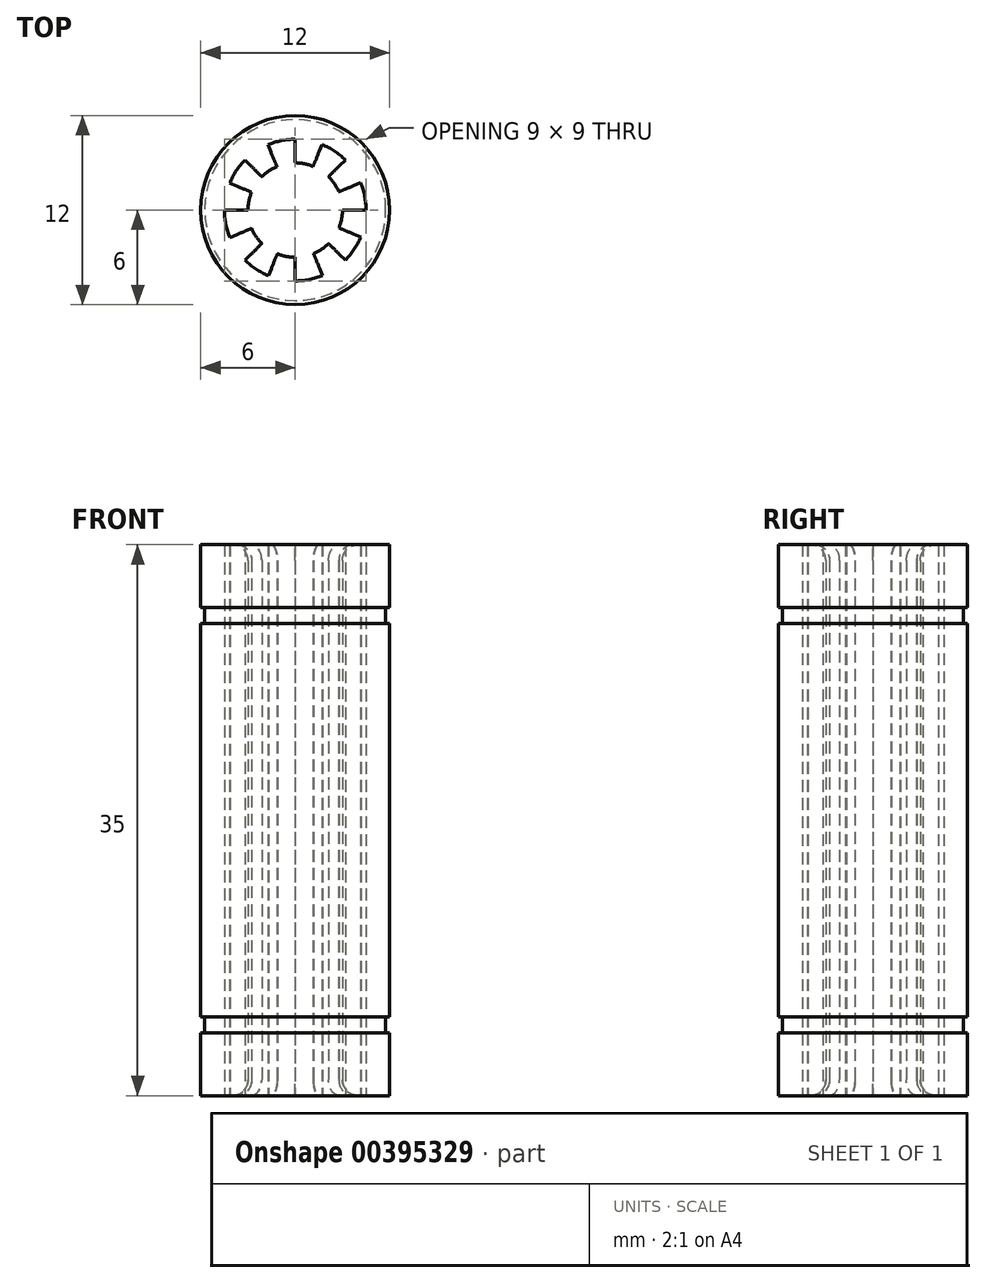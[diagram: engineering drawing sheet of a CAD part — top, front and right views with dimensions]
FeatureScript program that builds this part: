
annotation { "Feature Type Name" : "Feature", "Feature Type Description" : "" }
export const myFeature = defineFeature(function(context is Context, id is Id, definition is map)
    precondition{}
    {
        {
            var Q0;
            Q0=qCreatedBy(makeId("Top.planeOp"),FACE);
            var sketch = newSketch(context, id + "F0", { "sketchPlane" : qUnion([Q0])});
            skCircle(sketch, "E0", {"center": v(0, 0) * mm, "radius": 3 * mm});
            skCircle(sketch, "E1", {"center": v(0, 0) * mm, "radius": 6 * mm});
            skCircle(sketch, "E2", {"center": v(0, 0) * mm, "radius": 4.5 * mm});
            skLineSegment(sketch, "E3", {"start": v(0, 6) * mm, "end": v(0, -6) * mm});
            skLineSegment(sketch, "E4", {"start": v(-6, 0) * mm, "end": v(6, 0) * mm});
            skPoint(sketch, "E5", {"position": v(4.56, 3.9) * mm});
            skPoint(sketch, "E6", {"position": v(-4.24, 4.24) * mm});
            skPoint(sketch, "E7", {"position": v(-4.52, -3.95) * mm});
            skPoint(sketch, "E8", {"position": v(4.86, -3.52) * mm});
            skLineSegment(sketch, "E9", {"start": v(0, 0) * mm, "end": v(-4.24, 4.24) * mm});
            skPoint(sketch, "E10", {"position": v(-2.32, 5.53) * mm});
            skPoint(sketch, "E11", {"position": v(-5.54, 2.3) * mm});
            skLineSegment(sketch, "E12", {"start": v(-5.54, 2.3) * mm, "end": v(0, 0) * mm});
            skLineSegment(sketch, "E13", {"start": v(-2.32, 5.53) * mm, "end": v(0, 0) * mm});
            skSolve(sketch);
        }
        {
            var Q0;
            {var subQ0=sQuery(id+"F0.wireOp",EDGE,"E3");var subQ1=sQuery(id+"F0.wireOp",EDGE,"E1");var subQ2=makeQuery(id+"F0.imprint","INTERSECT",VERTEX,{"disambiguationData":[OD(0.0)],"derivedFrom":[subQ1,subQ0]});Q0=makeQuery(id+"F0.imprint","IMPRINT",FACE,{"disambiguationData":[TD([[makeQuery(id+"F0.imprint","IMPRINT",EDGE,{"disambiguationData":[TD([[subQ2,-1.0]])],"derivedFrom":subQ1}),1.0]])]});}
            var Q1;
            {var subQ0=sQuery(id+"F0.wireOp",EDGE,"E13");var subQ1=sQuery(id+"F0.wireOp",EDGE,"E0");var subQ2=makeQuery(id+"F0.imprint","INTERSECT",VERTEX,{"derivedFrom":[subQ1,subQ0]});Q1=makeQuery(id+"F0.imprint","IMPRINT",FACE,{"disambiguationData":[TD([[makeQuery(id+"F0.imprint","IMPRINT",EDGE,{"disambiguationData":[TD([[subQ2,-1.0]])],"derivedFrom":subQ1}),-1.0]])]});}
            var Q2;
            {var subQ0=sQuery(id+"F0.wireOp",EDGE,"E9");var subQ1=sQuery(id+"F0.wireOp",EDGE,"E1");var subQ2=makeQuery(id+"F0.imprint","INTERSECT",VERTEX,{"derivedFrom":[subQ1,subQ0]});Q2=makeQuery(id+"F0.imprint","IMPRINT",FACE,{"disambiguationData":[TD([[makeQuery(id+"F0.imprint","IMPRINT",EDGE,{"disambiguationData":[TD([[subQ2,1.0]])],"derivedFrom":subQ1}),1.0]])]});}
            extrude(context, id + "F1", {"entities" : qUnion([Q0, Q1, Q2]), "depth" : 35 * mm});
        }
        {
            var Q0;
            Q0=qCreatedBy(makeId("Front.planeOp"),FACE);
            var sketch = newSketch(context, id + "F2", { "sketchPlane" : qUnion([Q0])});
            skLineSegment(sketch, "E14", {"start": v(0, 46.48) * mm, "end": v(0, -20.09) * mm, "construction": true});
            skSolve(sketch);
        }
        {
            var Q0;
            Q0=makeQuery(id+"F1.opExtrude","SWEPT_BODY",BODY,{"disambiguationData":[OSD([sQuery(id+"F0.wireOp",EDGE,"E0"),sQuery(id+"F0.wireOp",EDGE,"E1"),sQuery(id+"F0.wireOp",EDGE,"E2"),sQuery(id+"F0.wireOp",EDGE,"E3"),sQuery(id+"F0.wireOp",EDGE,"E4"),sQuery(id+"F0.wireOp",EDGE,"E9")])]});
            var Q1;
            Q1=sQuery(id+"F2.wireOp",EDGE,"E14");
            circularPattern(context, id + "F3", {"entities" : qUnion([Q0]), "axis" : qUnion([Q1]), "angle" : 360 * degree, "instanceCount" : 8, "oppositeDirection" : true, "equalSpace" : true});
        }
        {
            var Q0;
            Q0=makeQuery(id+"F1.opExtrude","SWEPT_BODY",BODY,{"disambiguationData":[OSD([sQuery(id+"F0.wireOp",EDGE,"E0"),sQuery(id+"F0.wireOp",EDGE,"E1"),sQuery(id+"F0.wireOp",EDGE,"E2"),sQuery(id+"F0.wireOp",EDGE,"E3"),sQuery(id+"F0.wireOp",EDGE,"E9"),sQuery(id+"F0.wireOp",EDGE,"E13")])]});
            var Q1;
            Q1=makeQuery(id+"F3.opPattern","COPY",BODY,{"derivedFrom":makeQuery(id+"F1.opExtrude","SWEPT_BODY",BODY,{"disambiguationData":[OSD([sQuery(id+"F0.wireOp",EDGE,"E0"),sQuery(id+"F0.wireOp",EDGE,"E1"),sQuery(id+"F0.wireOp",EDGE,"E2"),sQuery(id+"F0.wireOp",EDGE,"E3"),sQuery(id+"F0.wireOp",EDGE,"E9"),sQuery(id+"F0.wireOp",EDGE,"E13")])]}),"instanceName":"1"});
            var Q2;
            Q2=makeQuery(id+"F3.opPattern","COPY",BODY,{"derivedFrom":makeQuery(id+"F1.opExtrude","SWEPT_BODY",BODY,{"disambiguationData":[OSD([sQuery(id+"F0.wireOp",EDGE,"E0"),sQuery(id+"F0.wireOp",EDGE,"E1"),sQuery(id+"F0.wireOp",EDGE,"E2"),sQuery(id+"F0.wireOp",EDGE,"E3"),sQuery(id+"F0.wireOp",EDGE,"E9"),sQuery(id+"F0.wireOp",EDGE,"E13")])]}),"instanceName":"2"});
            var Q3;
            Q3=makeQuery(id+"F3.opPattern","COPY",BODY,{"derivedFrom":makeQuery(id+"F1.opExtrude","SWEPT_BODY",BODY,{"disambiguationData":[OSD([sQuery(id+"F0.wireOp",EDGE,"E0"),sQuery(id+"F0.wireOp",EDGE,"E1"),sQuery(id+"F0.wireOp",EDGE,"E2"),sQuery(id+"F0.wireOp",EDGE,"E3"),sQuery(id+"F0.wireOp",EDGE,"E9"),sQuery(id+"F0.wireOp",EDGE,"E13")])]}),"instanceName":"3"});
            var Q4;
            Q4=makeQuery(id+"F3.opPattern","COPY",BODY,{"derivedFrom":makeQuery(id+"F1.opExtrude","SWEPT_BODY",BODY,{"disambiguationData":[OSD([sQuery(id+"F0.wireOp",EDGE,"E0"),sQuery(id+"F0.wireOp",EDGE,"E1"),sQuery(id+"F0.wireOp",EDGE,"E2"),sQuery(id+"F0.wireOp",EDGE,"E3"),sQuery(id+"F0.wireOp",EDGE,"E9"),sQuery(id+"F0.wireOp",EDGE,"E13")])]}),"instanceName":"4"});
            var Q5;
            Q5=makeQuery(id+"F3.opPattern","COPY",BODY,{"derivedFrom":makeQuery(id+"F1.opExtrude","SWEPT_BODY",BODY,{"disambiguationData":[OSD([sQuery(id+"F0.wireOp",EDGE,"E0"),sQuery(id+"F0.wireOp",EDGE,"E1"),sQuery(id+"F0.wireOp",EDGE,"E2"),sQuery(id+"F0.wireOp",EDGE,"E3"),sQuery(id+"F0.wireOp",EDGE,"E9"),sQuery(id+"F0.wireOp",EDGE,"E13")])]}),"instanceName":"5"});
            var Q6;
            Q6=makeQuery(id+"F3.opPattern","COPY",BODY,{"derivedFrom":makeQuery(id+"F1.opExtrude","SWEPT_BODY",BODY,{"disambiguationData":[OSD([sQuery(id+"F0.wireOp",EDGE,"E0"),sQuery(id+"F0.wireOp",EDGE,"E1"),sQuery(id+"F0.wireOp",EDGE,"E2"),sQuery(id+"F0.wireOp",EDGE,"E3"),sQuery(id+"F0.wireOp",EDGE,"E9"),sQuery(id+"F0.wireOp",EDGE,"E13")])]}),"instanceName":"6"});
            var Q7;
            Q7=makeQuery(id+"F3.opPattern","COPY",BODY,{"derivedFrom":makeQuery(id+"F1.opExtrude","SWEPT_BODY",BODY,{"disambiguationData":[OSD([sQuery(id+"F0.wireOp",EDGE,"E0"),sQuery(id+"F0.wireOp",EDGE,"E1"),sQuery(id+"F0.wireOp",EDGE,"E2"),sQuery(id+"F0.wireOp",EDGE,"E3"),sQuery(id+"F0.wireOp",EDGE,"E9"),sQuery(id+"F0.wireOp",EDGE,"E13")])]}),"instanceName":"7"});
            booleanBodies(context, id + "F4", {"operationType" : BooleanOperationType.UNION, "tools" : qUnion([Q0, Q1, Q2, Q3, Q4, Q5, Q6, Q7])});
        }
        {
            var Q0;
            Q0=makeQuery(id+"F3.opPattern","COPY",EDGE,{"derivedFrom":makeQuery(id+"F1.opExtrude","CAP_EDGE",EDGE,{"disambiguationData":[OSD([sQuery(id+"F0.wireOp",EDGE,"E0")])],"isStart":false}),"instanceName":"1"});
            var Q1;
            Q1=makeQuery(id+"F1.opExtrude","CAP_EDGE",EDGE,{"disambiguationData":[OSD([sQuery(id+"F0.wireOp",EDGE,"E0")])],"isStart":false});
            var Q2;
            Q2=makeQuery(id+"F3.opPattern","COPY",EDGE,{"derivedFrom":makeQuery(id+"F1.opExtrude","CAP_EDGE",EDGE,{"disambiguationData":[OSD([sQuery(id+"F0.wireOp",EDGE,"E0")])],"isStart":false}),"instanceName":"7"});
            var Q3;
            Q3=makeQuery(id+"F3.opPattern","COPY",EDGE,{"derivedFrom":makeQuery(id+"F1.opExtrude","CAP_EDGE",EDGE,{"disambiguationData":[OSD([sQuery(id+"F0.wireOp",EDGE,"E0")])],"isStart":false}),"instanceName":"6"});
            var Q4;
            Q4=makeQuery(id+"F3.opPattern","COPY",EDGE,{"derivedFrom":makeQuery(id+"F1.opExtrude","CAP_EDGE",EDGE,{"disambiguationData":[OSD([sQuery(id+"F0.wireOp",EDGE,"E0")])],"isStart":false}),"instanceName":"5"});
            var Q5;
            Q5=makeQuery(id+"F3.opPattern","COPY",EDGE,{"derivedFrom":makeQuery(id+"F1.opExtrude","CAP_EDGE",EDGE,{"disambiguationData":[OSD([sQuery(id+"F0.wireOp",EDGE,"E0")])],"isStart":false}),"instanceName":"4"});
            var Q6;
            Q6=makeQuery(id+"F3.opPattern","COPY",EDGE,{"derivedFrom":makeQuery(id+"F1.opExtrude","CAP_EDGE",EDGE,{"disambiguationData":[OSD([sQuery(id+"F0.wireOp",EDGE,"E0")])],"isStart":false}),"instanceName":"3"});
            var Q7;
            Q7=makeQuery(id+"F3.opPattern","COPY",EDGE,{"derivedFrom":makeQuery(id+"F1.opExtrude","CAP_EDGE",EDGE,{"disambiguationData":[OSD([sQuery(id+"F0.wireOp",EDGE,"E0")])],"isStart":false}),"instanceName":"2"});
            var Q8;
            Q8=makeQuery(id+"F3.opPattern","COPY",EDGE,{"derivedFrom":makeQuery(id+"F1.opExtrude","CAP_EDGE",EDGE,{"disambiguationData":[OSD([sQuery(id+"F0.wireOp",EDGE,"E0")])],"isStart":true}),"instanceName":"5"});
            var Q9;
            Q9=makeQuery(id+"F3.opPattern","COPY",EDGE,{"derivedFrom":makeQuery(id+"F1.opExtrude","CAP_EDGE",EDGE,{"disambiguationData":[OSD([sQuery(id+"F0.wireOp",EDGE,"E0")])],"isStart":true}),"instanceName":"6"});
            var Q10;
            Q10=makeQuery(id+"F3.opPattern","COPY",EDGE,{"derivedFrom":makeQuery(id+"F1.opExtrude","CAP_EDGE",EDGE,{"disambiguationData":[OSD([sQuery(id+"F0.wireOp",EDGE,"E0")])],"isStart":true}),"instanceName":"7"});
            var Q11;
            Q11=makeQuery(id+"F1.opExtrude","CAP_EDGE",EDGE,{"disambiguationData":[OSD([sQuery(id+"F0.wireOp",EDGE,"E0")])],"isStart":true});
            var Q12;
            Q12=makeQuery(id+"F3.opPattern","COPY",EDGE,{"derivedFrom":makeQuery(id+"F1.opExtrude","CAP_EDGE",EDGE,{"disambiguationData":[OSD([sQuery(id+"F0.wireOp",EDGE,"E0")])],"isStart":true}),"instanceName":"1"});
            var Q13;
            Q13=makeQuery(id+"F3.opPattern","COPY",EDGE,{"derivedFrom":makeQuery(id+"F1.opExtrude","CAP_EDGE",EDGE,{"disambiguationData":[OSD([sQuery(id+"F0.wireOp",EDGE,"E0")])],"isStart":true}),"instanceName":"2"});
            var Q14;
            Q14=makeQuery(id+"F3.opPattern","COPY",EDGE,{"derivedFrom":makeQuery(id+"F1.opExtrude","CAP_EDGE",EDGE,{"disambiguationData":[OSD([sQuery(id+"F0.wireOp",EDGE,"E0")])],"isStart":true}),"instanceName":"3"});
            var Q15;
            Q15=makeQuery(id+"F3.opPattern","COPY",EDGE,{"derivedFrom":makeQuery(id+"F1.opExtrude","CAP_EDGE",EDGE,{"disambiguationData":[OSD([sQuery(id+"F0.wireOp",EDGE,"E0")])],"isStart":true}),"instanceName":"4"});
            fillet(context, id + "F5", {"entities" : qUnion([Q0, Q1, Q2, Q3, Q4, Q5, Q6, Q7, Q8, Q9, Q10, Q11, Q12, Q13, Q14, Q15]), "radius" : 1 * mm, "tangentPropagation" : true, "allowEdgeOverflow" : false});
        }
        {
            var Q0;
            {var subQ0=makeQuery(id+"F1.opExtrude","CAP_FACE",FACE,{"disambiguationData":[OSD([sQuery(id+"F0.wireOp",EDGE,"E0"),sQuery(id+"F0.wireOp",EDGE,"E1"),sQuery(id+"F0.wireOp",EDGE,"E2"),sQuery(id+"F0.wireOp",EDGE,"E3"),sQuery(id+"F0.wireOp",EDGE,"E9"),sQuery(id+"F0.wireOp",EDGE,"E13")])],"isStart":false});Q0=makeQuery(id+"F4.opBoolean","MERGE",FACE,{"derivedFrom":[subQ0,makeQuery(id+"F3.opPattern","COPY",FACE,{"derivedFrom":subQ0,"instanceName":"1"}),makeQuery(id+"F3.opPattern","COPY",FACE,{"derivedFrom":subQ0,"instanceName":"2"}),makeQuery(id+"F3.opPattern","COPY",FACE,{"derivedFrom":subQ0,"instanceName":"3"}),makeQuery(id+"F3.opPattern","COPY",FACE,{"derivedFrom":subQ0,"instanceName":"4"}),makeQuery(id+"F3.opPattern","COPY",FACE,{"derivedFrom":subQ0,"instanceName":"5"}),makeQuery(id+"F3.opPattern","COPY",FACE,{"derivedFrom":subQ0,"instanceName":"6"}),makeQuery(id+"F3.opPattern","COPY",FACE,{"derivedFrom":subQ0,"instanceName":"7"})]});}
            cPlane(context, id + "F6", {"entities" : qUnion([Q0]), "cplaneType" : CPlaneType.OFFSET, "offset" : 4 * mm, "oppositeDirection" : true, "width" : 150 * mm, "height" : 150 * mm});
        }
        {
            var Q0;
            Q0=qCreatedBy(id+"F6.planeOp",FACE);
            var sketch = newSketch(context, id + "F7", { "sketchPlane" : qUnion([Q0])});
            skCircle(sketch, "E15", {"center": v(0, 0) * mm, "radius": 5.75 * mm});
            skCircle(sketch, "E16", {"center": v(0, 0) * mm, "radius": 6.48 * mm});
            skSolve(sketch);
        }
        {
            var Q0;
            Q0 = qSketchRegion(id + "F7", true);
            extrude(context, id + "F8", {"entities" : qUnion([Q0]), "operationType" : NewBodyOperationType.REMOVE, "oppositeDirection" : true, "depth" : 1 * mm});
        }
        {
            var Q0;
            {var subQ0=makeQuery(id+"F1.opExtrude","CAP_FACE",FACE,{"disambiguationData":[OSD([sQuery(id+"F0.wireOp",EDGE,"E0"),sQuery(id+"F0.wireOp",EDGE,"E1"),sQuery(id+"F0.wireOp",EDGE,"E2"),sQuery(id+"F0.wireOp",EDGE,"E3"),sQuery(id+"F0.wireOp",EDGE,"E9"),sQuery(id+"F0.wireOp",EDGE,"E13")])],"isStart":true});Q0=makeQuery(id+"F4.opBoolean","MERGE",FACE,{"derivedFrom":[subQ0,makeQuery(id+"F3.opPattern","COPY",FACE,{"derivedFrom":subQ0,"instanceName":"1"}),makeQuery(id+"F3.opPattern","COPY",FACE,{"derivedFrom":subQ0,"instanceName":"2"}),makeQuery(id+"F3.opPattern","COPY",FACE,{"derivedFrom":subQ0,"instanceName":"3"}),makeQuery(id+"F3.opPattern","COPY",FACE,{"derivedFrom":subQ0,"instanceName":"4"}),makeQuery(id+"F3.opPattern","COPY",FACE,{"derivedFrom":subQ0,"instanceName":"5"}),makeQuery(id+"F3.opPattern","COPY",FACE,{"derivedFrom":subQ0,"instanceName":"6"}),makeQuery(id+"F3.opPattern","COPY",FACE,{"derivedFrom":subQ0,"instanceName":"7"})]});}
            cPlane(context, id + "F9", {"entities" : qUnion([Q0]), "cplaneType" : CPlaneType.OFFSET, "offset" : 4 * mm, "oppositeDirection" : true, "width" : 150 * mm, "height" : 150 * mm});
        }
        {
            var Q0;
            Q0=qCreatedBy(id+"F9.planeOp",FACE);
            var sketch = newSketch(context, id + "F10", { "sketchPlane" : qUnion([Q0])});
            skCircle(sketch, "E17", {"center": v(0, 0) * mm, "radius": 5.75 * mm});
            skCircle(sketch, "E18", {"center": v(0, 0) * mm, "radius": 6.41 * mm});
            skSolve(sketch);
        }
        {
            var Q0;
            Q0 = qSketchRegion(id + "F10", true);
            extrude(context, id + "F11", {"entities" : qUnion([Q0]), "operationType" : NewBodyOperationType.REMOVE, "oppositeDirection" : true, "depth" : 1 * mm});
        }
    });
